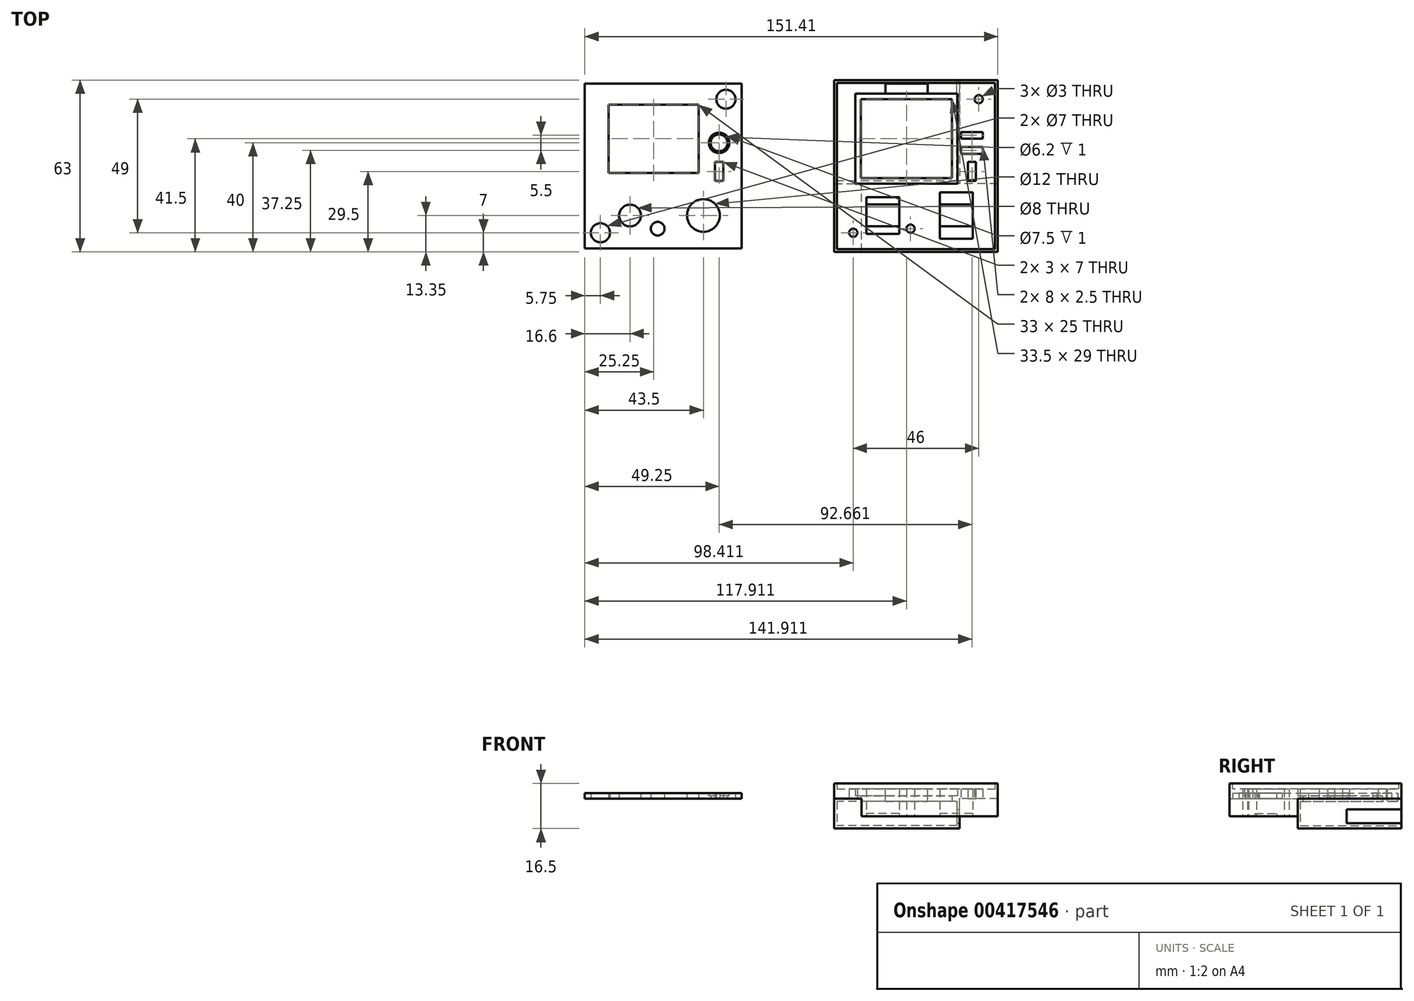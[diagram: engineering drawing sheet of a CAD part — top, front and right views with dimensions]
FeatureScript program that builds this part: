
annotation { "Feature Type Name" : "Feature", "Feature Type Description" : "" }
export const myFeature = defineFeature(function(context is Context, id is Id, definition is map)
    precondition{}
    {
        {
            var Q0;
            Q0=qCreatedBy(makeId("Top.planeOp"),FACE);
            var sketch = newSketch(context, id + "F0", { "sketchPlane" : qUnion([Q0])});
            skPoint(sketch, "E0.middle", {"position": v(0, 0) * mm});
            skLineSegment(sketch, "E1.bottom", {"start": v(13, -2.5) * mm, "end": v(-20, -2.5) * mm});
            skLineSegment(sketch, "E1.top", {"start": v(13, 22.5) * mm, "end": v(-20, 22.5) * mm});
            skLineSegment(sketch, "E1.left", {"start": v(13, -2.5) * mm, "end": v(13, 22.5) * mm});
            skLineSegment(sketch, "E1.right", {"start": v(-20, -2.5) * mm, "end": v(-20, 22.5) * mm});
            skCircle(sketch, "E2", {"center": v(14.75, -18.15) * mm, "radius": 6 * mm});
            skCircle(sketch, "E3", {"center": v(-12.15, -18.15) * mm, "radius": 4 * mm});
            skCircle(sketch, "E4", {"center": v(-2, -23) * mm, "radius": 2.5 * mm});
            skPoint(sketch, "E5", {"position": v(-3.5, 10) * mm});
            skPoint(sketch, "E5.positionSnap0", {"position": v(-3.5, 22.5) * mm});
            skPoint(sketch, "E5.positionSnap1", {"position": v(-20, 10) * mm});
            skCircle(sketch, "E6", {"center": v(-23, -24.5) * mm, "radius": 3.5 * mm});
            skCircle(sketch, "E7", {"center": v(23, 24.5) * mm, "radius": 3.5 * mm});
            skLineSegment(sketch, "E8.bottom", {"start": v(28.75, -30.25) * mm, "end": v(-28.75, -30.25) * mm});
            skLineSegment(sketch, "E8.top", {"start": v(28.75, 30.25) * mm, "end": v(-28.75, 30.25) * mm});
            skLineSegment(sketch, "E8.left", {"start": v(28.75, -30.25) * mm, "end": v(28.75, 30.25) * mm});
            skLineSegment(sketch, "E8.right", {"start": v(-28.75, -30.25) * mm, "end": v(-28.75, 30.25) * mm});
            skCircle(sketch, "E9", {"center": v(20.5, 8.5) * mm, "radius": 3.75 * mm, "construction": true});
            skCircle(sketch, "E10", {"center": v(20.5, 8.5) * mm, "radius": 3.1 * mm});
            skLineSegment(sketch, "E11.bottom", {"start": v(22, -5.5) * mm, "end": v(19, -5.5) * mm});
            skLineSegment(sketch, "E11.top", {"start": v(22, 1.5) * mm, "end": v(19, 1.5) * mm});
            skLineSegment(sketch, "E11.left", {"start": v(22, -5.5) * mm, "end": v(22, 1.5) * mm});
            skLineSegment(sketch, "E11.right", {"start": v(19, -5.5) * mm, "end": v(19, 1.5) * mm});
            skPoint(sketch, "E11.middle", {"position": v(20.5, -2) * mm});
            skSolve(sketch);
        }
        {
            var Q0;
            Q0=qCreatedBy(makeId("Top.planeOp"),FACE);
            var sketch = newSketch(context, id + "F1", { "sketchPlane" : qUnion([Q0])});
            skLineSegment(sketch, "E12.bottom", {"start": v(122.66, -31.5) * mm, "end": v(62.66, -31.5) * mm});
            skLineSegment(sketch, "E12.top", {"start": v(122.66, 31.5) * mm, "end": v(62.66, 31.5) * mm});
            skLineSegment(sketch, "E12.left", {"start": v(122.66, -31.5) * mm, "end": v(122.66, 31.5) * mm});
            skLineSegment(sketch, "E12.right", {"start": v(62.66, -31.5) * mm, "end": v(62.66, 31.5) * mm});
            skPoint(sketch, "E12.middle", {"position": v(92.66, 0) * mm});
            skLineSegment(sketch, "E13.bottom", {"start": v(107.91, -6.5) * mm, "end": v(70.41, -6.5) * mm});
            skLineSegment(sketch, "E13.top", {"start": v(107.91, 26.5) * mm, "end": v(70.41, 26.5) * mm});
            skLineSegment(sketch, "E13.left", {"start": v(107.91, -6.5) * mm, "end": v(107.91, 26.5) * mm});
            skLineSegment(sketch, "E13.right", {"start": v(70.41, -6.5) * mm, "end": v(70.41, 26.5) * mm});
            skCircle(sketch, "E14", {"center": v(69.66, -24.5) * mm, "radius": 1.5 * mm});
            skCircle(sketch, "E15", {"center": v(115.66, 24.5) * mm, "radius": 1.5 * mm});
            skCircle(sketch, "E16", {"center": v(107.41, -18.15) * mm, "radius": 6.1 * mm, "construction": true});
            skLineSegment(sketch, "E17.bottom", {"start": v(111.66, 1.5) * mm, "end": v(114.66, 1.5) * mm});
            skLineSegment(sketch, "E17.top", {"start": v(111.66, -5.5) * mm, "end": v(114.66, -5.5) * mm});
            skLineSegment(sketch, "E17.left", {"start": v(111.66, 1.5) * mm, "end": v(111.66, -5.5) * mm});
            skLineSegment(sketch, "E17.right", {"start": v(114.66, 1.5) * mm, "end": v(114.66, -5.5) * mm});
            skPoint(sketch, "E18.centerSnap0", {"position": v(113.16, 1.5) * mm});
            skCircle(sketch, "E19", {"center": v(80.51, -18.15) * mm, "radius": 2.5 * mm, "construction": true});
            skCircle(sketch, "E20", {"center": v(90.66, -23) * mm, "radius": 1.5 * mm});
            skLineSegment(sketch, "E21.bottom", {"start": v(113.41, -26.65) * mm, "end": v(101.41, -26.65) * mm});
            skLineSegment(sketch, "E21.top", {"start": v(113.41, -9.65) * mm, "end": v(101.41, -9.65) * mm});
            skLineSegment(sketch, "E21.left", {"start": v(113.41, -26.65) * mm, "end": v(113.41, -9.65) * mm});
            skLineSegment(sketch, "E21.right", {"start": v(101.41, -26.65) * mm, "end": v(101.41, -9.65) * mm});
            skLineSegment(sketch, "E22.bottom", {"start": v(115.66, 6) * mm, "end": v(110.66, 6) * mm, "construction": true});
            skLineSegment(sketch, "E22.top", {"start": v(115.66, 11) * mm, "end": v(110.66, 11) * mm, "construction": true});
            skLineSegment(sketch, "E22.left", {"start": v(115.66, 6) * mm, "end": v(115.66, 11) * mm, "construction": true});
            skLineSegment(sketch, "E22.right", {"start": v(110.66, 6) * mm, "end": v(110.66, 11) * mm, "construction": true});
            skPoint(sketch, "E22.middle", {"position": v(113.16, 8.5) * mm});
            skPoint(sketch, "E23", {"position": v(89.16, 10) * mm});
            skPoint(sketch, "E23.positionSnap0", {"position": v(89.16, 26.5) * mm});
            skPoint(sketch, "E23.positionSnap1", {"position": v(70.41, 10) * mm});
            skLineSegment(sketch, "E24.bottom", {"start": v(117.16, 4.5) * mm, "end": v(109.16, 4.5) * mm});
            skLineSegment(sketch, "E24.top", {"start": v(117.16, 12.5) * mm, "end": v(109.16, 12.5) * mm});
            skLineSegment(sketch, "E24.left", {"start": v(117.16, 4.5) * mm, "end": v(117.16, 12.5) * mm});
            skLineSegment(sketch, "E24.right", {"start": v(109.16, 4.5) * mm, "end": v(109.16, 12.5) * mm});
            skCircle(sketch, "E25", {"center": v(69.66, -24.5) * mm, "radius": 3.5 * mm, "construction": true});
            skCircle(sketch, "E26", {"center": v(115.66, 24.5) * mm, "radius": 3.5 * mm, "construction": true});
            skLineSegment(sketch, "E27.bottom", {"start": v(121.41, -30.25) * mm, "end": v(63.91, -30.25) * mm, "construction": true});
            skLineSegment(sketch, "E27.top", {"start": v(121.41, 30.25) * mm, "end": v(63.91, 30.25) * mm, "construction": true});
            skLineSegment(sketch, "E27.left", {"start": v(121.41, -30.25) * mm, "end": v(121.41, 30.25) * mm, "construction": true});
            skLineSegment(sketch, "E27.right", {"start": v(63.91, -30.25) * mm, "end": v(63.91, 30.25) * mm, "construction": true});
            skLineSegment(sketch, "E28.bottom", {"start": v(86.51, -24.9) * mm, "end": v(74.51, -24.9) * mm});
            skLineSegment(sketch, "E28.top", {"start": v(86.51, -11.4) * mm, "end": v(74.51, -11.4) * mm});
            skLineSegment(sketch, "E28.left", {"start": v(86.51, -24.9) * mm, "end": v(86.51, -11.4) * mm});
            skLineSegment(sketch, "E28.right", {"start": v(74.51, -24.9) * mm, "end": v(74.51, -11.4) * mm});
            skLineSegment(sketch, "E29.bottom", {"start": v(86.51, -22.15) * mm, "end": v(74.51, -22.15) * mm});
            skLineSegment(sketch, "E29.top", {"start": v(86.51, -14.15) * mm, "end": v(74.51, -14.15) * mm});
            skLineSegment(sketch, "E29.left", {"start": v(86.51, -22.15) * mm, "end": v(86.51, -14.15) * mm});
            skLineSegment(sketch, "E29.right", {"start": v(74.51, -22.15) * mm, "end": v(74.51, -14.15) * mm});
            skLineSegment(sketch, "E30.bottom", {"start": v(113.41, -22.15) * mm, "end": v(101.41, -22.15) * mm});
            skLineSegment(sketch, "E30.top", {"start": v(113.41, -14.15) * mm, "end": v(101.41, -14.15) * mm});
            skLineSegment(sketch, "E30.left", {"start": v(113.41, -22.15) * mm, "end": v(113.41, -14.15) * mm});
            skLineSegment(sketch, "E30.right", {"start": v(101.41, -22.15) * mm, "end": v(101.41, -14.15) * mm});
            skLineSegment(sketch, "E31.bottom", {"start": v(117.16, 7) * mm, "end": v(109.16, 7) * mm});
            skLineSegment(sketch, "E31.top", {"start": v(117.16, 10) * mm, "end": v(109.16, 10) * mm});
            skLineSegment(sketch, "E31.left", {"start": v(117.16, 7) * mm, "end": v(117.16, 10) * mm});
            skLineSegment(sketch, "E31.right", {"start": v(109.16, 7) * mm, "end": v(109.16, 10) * mm});
            skSolve(sketch);
        }
        {
            var Q0;
            Q0=makeQuery(id+"F1.imprint","IMPRINT",FACE,{"disambiguationData":[TD([[makeQuery(id+"F1.imprint","IMPRINT",EDGE,{"derivedFrom":sQuery(id+"F1.wireOp",EDGE,"E12.bottom")}),-1.0]])]});
            var Q1;
            Q1=makeQuery(id+"F1.imprint","IMPRINT",FACE,{"disambiguationData":[TD([[makeQuery(id+"F1.imprint","IMPRINT",EDGE,{"derivedFrom":sQuery(id+"F1.wireOp",EDGE,"E29.bottom")}),-1.0]])]});
            var Q2;
            Q2=makeQuery(id+"F1.imprint","IMPRINT",FACE,{"disambiguationData":[TD([[makeQuery(id+"F1.imprint","IMPRINT",EDGE,{"derivedFrom":sQuery(id+"F1.wireOp",EDGE,"E30.bottom")}),-1.0]])]});
            var Q3;
            Q3=makeQuery(id+"F1.imprint","IMPRINT",FACE,{"disambiguationData":[TD([[makeQuery(id+"F1.imprint","IMPRINT",EDGE,{"derivedFrom":sQuery(id+"F1.wireOp",EDGE,"E31.bottom")}),-1.0]])]});
            extrude(context, id + "F2", {"entities" : qUnion([Q0, Q1, Q2, Q3]), "depth" : 3.5 * mm});
        }
        {
            var Q0;
            Q0=makeQuery(id+"F2.opExtrude","CAP_FACE",FACE,{"disambiguationData":[OSD([sQuery(id+"F1.wireOp",EDGE,"E12.bottom"),sQuery(id+"F1.wireOp",EDGE,"E12.top"),sQuery(id+"F1.wireOp",EDGE,"E12.left"),sQuery(id+"F1.wireOp",EDGE,"E12.right"),sQuery(id+"F1.wireOp",EDGE,"E13.bottom"),sQuery(id+"F1.wireOp",EDGE,"E13.top"),sQuery(id+"F1.wireOp",EDGE,"E13.left"),sQuery(id+"F1.wireOp",EDGE,"E13.right"),sQuery(id+"F1.wireOp",EDGE,"E14"),sQuery(id+"F1.wireOp",EDGE,"E15"),sQuery(id+"F1.wireOp",EDGE,"E16"),sQuery(id+"F1.wireOp",EDGE,"E17.bottom"),sQuery(id+"F1.wireOp",EDGE,"E17.top"),sQuery(id+"F1.wireOp",EDGE,"E17.left"),sQuery(id+"F1.wireOp",EDGE,"E17.right"),sQuery(id+"F1.wireOp",EDGE,"E18"),sQuery(id+"F1.wireOp",EDGE,"E19"),sQuery(id+"F1.wireOp",EDGE,"E20")])],"isStart":false});
            var sketch = newSketch(context, id + "F3", { "sketchPlane" : qUnion([Q0])});
            skLineSegment(sketch, "E32.bottom", {"start": v(96.91, 26.5) * mm, "end": v(81.41, 26.5) * mm});
            skLineSegment(sketch, "E32.top", {"start": v(96.91, 30.25) * mm, "end": v(81.41, 30.25) * mm});
            skLineSegment(sketch, "E32.left", {"start": v(96.91, 26.5) * mm, "end": v(96.91, 30.25) * mm});
            skLineSegment(sketch, "E32.right", {"start": v(81.41, 26.5) * mm, "end": v(81.41, 30.25) * mm});
            skPoint(sketch, "E32.middle", {"position": v(89.16, 28.38) * mm});
            skPoint(sketch, "E32.middle.positionSnap0", {"position": v(89.16, 26.5) * mm});
            skPoint(sketch, "E32.centerSnap0", {"position": v(89.16, 26.5) * mm});
            skSolve(sketch);
        }
        {
            var Q0;
            Q0=makeQuery(id+"F2.opExtrude","CAP_FACE",FACE,{"disambiguationData":[OSD([sQuery(id+"F1.wireOp",EDGE,"E12.bottom"),sQuery(id+"F1.wireOp",EDGE,"E12.top"),sQuery(id+"F1.wireOp",EDGE,"E12.left"),sQuery(id+"F1.wireOp",EDGE,"E12.right"),sQuery(id+"F1.wireOp",EDGE,"E13.bottom"),sQuery(id+"F1.wireOp",EDGE,"E13.top"),sQuery(id+"F1.wireOp",EDGE,"E13.left"),sQuery(id+"F1.wireOp",EDGE,"E13.right"),sQuery(id+"F1.wireOp",EDGE,"E14"),sQuery(id+"F1.wireOp",EDGE,"E15"),sQuery(id+"F1.wireOp",EDGE,"E16"),sQuery(id+"F1.wireOp",EDGE,"E17.bottom"),sQuery(id+"F1.wireOp",EDGE,"E17.top"),sQuery(id+"F1.wireOp",EDGE,"E17.left"),sQuery(id+"F1.wireOp",EDGE,"E17.right"),sQuery(id+"F1.wireOp",EDGE,"E18"),sQuery(id+"F1.wireOp",EDGE,"E19"),sQuery(id+"F1.wireOp",EDGE,"E20")])],"isStart":true});
            var sketch = newSketch(context, id + "F4", { "sketchPlane" : qUnion([Q0])});
            skLineSegment(sketch, "E33.bottom", {"start": v(70.41, -26.5) * mm, "end": v(107.91, -26.5) * mm});
            skLineSegment(sketch, "E33.top", {"start": v(70.41, 6.5) * mm, "end": v(107.91, 6.5) * mm});
            skLineSegment(sketch, "E33.left", {"start": v(70.41, -26.5) * mm, "end": v(70.41, 6.5) * mm});
            skLineSegment(sketch, "E33.right", {"start": v(107.91, -26.5) * mm, "end": v(107.91, 6.5) * mm});
            skLineSegment(sketch, "E34.0", {"start": v(105.91, -24.5) * mm, "end": v(105.91, 4.5) * mm});
            skLineSegment(sketch, "E34.1", {"start": v(72.41, -24.5) * mm, "end": v(105.91, -24.5) * mm});
            skLineSegment(sketch, "E34.2", {"start": v(72.41, -24.5) * mm, "end": v(72.41, 4.5) * mm});
            skLineSegment(sketch, "E34.3", {"start": v(72.41, 4.5) * mm, "end": v(105.91, 4.5) * mm});
            skSolve(sketch);
        }
        {
            var Q0;
            Q0=makeQuery(id+"F4.imprint","IMPRINT",FACE,{"disambiguationData":[TD([[makeQuery(id+"F4.imprint","IMPRINT",EDGE,{"derivedFrom":sQuery(id+"F4.wireOp",EDGE,"E33.bottom")}),-1.0]])]});
            extrude(context, id + "F5", {"entities" : qUnion([Q0]), "operationType" : NewBodyOperationType.ADD, "oppositeDirection" : true, "depth" : 1 * mm});
        }
        {
            var Q0;
            Q0=makeQuery(id+"F3.imprint","IMPRINT",FACE,{"disambiguationData":[TD([[makeQuery(id+"F3.imprint","IMPRINT",EDGE,{"derivedFrom":sQuery(id+"F3.wireOp",EDGE,"E32.bottom")}),-1.0]])]});
            extrude(context, id + "F6", {"entities" : qUnion([Q0]), "operationType" : NewBodyOperationType.REMOVE, "oppositeDirection" : true, "depth" : 2.5 * mm});
        }
        {
            var Q0;
            Q0=makeQuery(id+"F5.boolean.opBoolean","MERGE",FACE,{"derivedFrom":[makeQuery(id+"F2.opExtrude","CAP_FACE",FACE,{"disambiguationData":[OSD([sQuery(id+"F1.wireOp",EDGE,"E12.bottom"),sQuery(id+"F1.wireOp",EDGE,"E12.top"),sQuery(id+"F1.wireOp",EDGE,"E12.left"),sQuery(id+"F1.wireOp",EDGE,"E12.right"),sQuery(id+"F1.wireOp",EDGE,"E13.bottom"),sQuery(id+"F1.wireOp",EDGE,"E13.top"),sQuery(id+"F1.wireOp",EDGE,"E13.left"),sQuery(id+"F1.wireOp",EDGE,"E13.right"),sQuery(id+"F1.wireOp",EDGE,"E14"),sQuery(id+"F1.wireOp",EDGE,"E15"),sQuery(id+"F1.wireOp",EDGE,"E16"),sQuery(id+"F1.wireOp",EDGE,"E17.bottom"),sQuery(id+"F1.wireOp",EDGE,"E17.top"),sQuery(id+"F1.wireOp",EDGE,"E17.left"),sQuery(id+"F1.wireOp",EDGE,"E17.right"),sQuery(id+"F1.wireOp",EDGE,"E18"),sQuery(id+"F1.wireOp",EDGE,"E19"),sQuery(id+"F1.wireOp",EDGE,"E20")])],"isStart":true}),makeQuery(id+"F5.opExtrude","CAP_FACE",FACE,{"disambiguationData":[OSD([sQuery(id+"F4.wireOp",EDGE,"E33.bottom"),sQuery(id+"F4.wireOp",EDGE,"E33.top"),sQuery(id+"F4.wireOp",EDGE,"E33.left"),sQuery(id+"F4.wireOp",EDGE,"E33.right"),sQuery(id+"F4.wireOp",EDGE,"E34.0"),sQuery(id+"F4.wireOp",EDGE,"E34.1"),sQuery(id+"F4.wireOp",EDGE,"E34.2"),sQuery(id+"F4.wireOp",EDGE,"E34.3")])],"isStart":true})]});
            var sketch = newSketch(context, id + "F7", { "sketchPlane" : qUnion([Q0])});
            skLineSegment(sketch, "E35.bottom", {"start": v(114.91, -31.5) * mm, "end": v(67.91, -31.5) * mm, "construction": true});
            skLineSegment(sketch, "E35.top", {"start": v(114.91, 0.5) * mm, "end": v(67.91, 0.5) * mm, "construction": true});
            skLineSegment(sketch, "E35.left", {"start": v(114.91, -31.5) * mm, "end": v(114.91, 0.5) * mm, "construction": true});
            skLineSegment(sketch, "E35.right", {"start": v(67.91, -31.5) * mm, "end": v(67.91, 0.5) * mm, "construction": true});
            skSolve(sketch);
        }
        {
            var Q0;
            Q0=makeQuery(id+"F0.imprint","IMPRINT",FACE,{"disambiguationData":[TD([[makeQuery(id+"F0.imprint","IMPRINT",EDGE,{"derivedFrom":sQuery(id+"F0.wireOp",EDGE,"E1.bottom")}),1.0]])]});
            var Q1;
            {var subQ3=sQuery(id+"F0.wireOp",EDGE,"XrDQp62H-MWh6-TRDE-LRBF-NnkS5WIpAHLl.bottom");Q1=makeQuery(id+"F0.imprint","IMPRINT",FACE,{"disambiguationData":[TD([[makeQuery(id+"F0.imprint","IMPRINT",EDGE,{"derivedFrom":subQ3}),-1.0]])]});}
            var Q2;
            {var subQ0=sQuery(id+"F0.wireOp",EDGE,"2c6vpU0J-e8TA-CdwJ-wqkp-RvG89t70vTgT.bottom");Q2=makeQuery(id+"F0.imprint","IMPRINT",FACE,{"disambiguationData":[TD([[makeQuery(id+"F0.imprint","IMPRINT",EDGE,{"derivedFrom":subQ0}),1.0]])]});}
            var Q3;
            {var subQ3=sQuery(id+"F0.wireOp",EDGE,"BUTc56Jz-DEV2-YpXM-oIQJ-WA8c8EbTXwWs.bottom");Q3=makeQuery(id+"F0.imprint","IMPRINT",FACE,{"disambiguationData":[TD([[makeQuery(id+"F0.imprint","IMPRINT",EDGE,{"derivedFrom":subQ3}),1.0]])]});}
            var Q4;
            {var subQ0=sQuery(id+"F0.wireOp",EDGE,"JL6GV5r3-Ixaj-ni79-uZlj-3xSKczFOYfCu.bottom");Q4=makeQuery(id+"F0.imprint","IMPRINT",FACE,{"disambiguationData":[TD([[makeQuery(id+"F0.imprint","IMPRINT",EDGE,{"derivedFrom":subQ0}),-1.0]])]});}
            extrude(context, id + "F8", {"entities" : qUnion([Q0, Q1, Q2, Q3, Q4]), "depth" : 2 * mm});
        }
        {
            var Q0;
            Q0=makeQuery(id+"F8.opExtrude","CAP_FACE",FACE,{"disambiguationData":[OSD([sQuery(id+"F0.wireOp",EDGE,"E1.bottom"),sQuery(id+"F0.wireOp",EDGE,"E1.top"),sQuery(id+"F0.wireOp",EDGE,"E1.left"),sQuery(id+"F0.wireOp",EDGE,"E1.right"),sQuery(id+"F0.wireOp",EDGE,"2c6vpU0J-e8TA-CdwJ-wqkp-RvG89t70vTgT.top"),sQuery(id+"F0.wireOp",EDGE,"JL6GV5r3-Ixaj-ni79-uZlj-3xSKczFOYfCu.top"),sQuery(id+"F0.wireOp",EDGE,"XrDQp62H-MWh6-TRDE-LRBF-NnkS5WIpAHLl.bottom"),sQuery(id+"F0.wireOp",EDGE,"XrDQp62H-MWh6-TRDE-LRBF-NnkS5WIpAHLl.top"),sQuery(id+"F0.wireOp",EDGE,"XrDQp62H-MWh6-TRDE-LRBF-NnkS5WIpAHLl.right"),sQuery(id+"F0.wireOp",EDGE,"BUTc56Jz-DEV2-YpXM-oIQJ-WA8c8EbTXwWs.bottom"),sQuery(id+"F0.wireOp",EDGE,"BUTc56Jz-DEV2-YpXM-oIQJ-WA8c8EbTXwWs.top"),sQuery(id+"F0.wireOp",EDGE,"BUTc56Jz-DEV2-YpXM-oIQJ-WA8c8EbTXwWs.right"),sQuery(id+"F0.wireOp",EDGE,"E2"),sQuery(id+"F0.wireOp",EDGE,"E3"),sQuery(id+"F0.wireOp",EDGE,"E4")])],"isStart":false});
            var sketch = newSketch(context, id + "F9", { "sketchPlane" : qUnion([Q0])});
            skLineSegment(sketch, "E36.bottom", {"start": v(-20, 22.5) * mm, "end": v(13, 22.5) * mm});
            skLineSegment(sketch, "E36.top", {"start": v(-20, 23.5) * mm, "end": v(13, 23.5) * mm});
            skLineSegment(sketch, "E36.left", {"start": v(-20, 22.5) * mm, "end": v(-20, 23.5) * mm});
            skLineSegment(sketch, "E36.right", {"start": v(13, 22.5) * mm, "end": v(13, 23.5) * mm});
            skLineSegment(sketch, "E37.bottom", {"start": v(-20, 23.5) * mm, "end": v(-21, 23.5) * mm});
            skLineSegment(sketch, "E37.top", {"start": v(-20, -2.5) * mm, "end": v(-21, -2.5) * mm});
            skLineSegment(sketch, "E37.left", {"start": v(-20, 23.5) * mm, "end": v(-20, -2.5) * mm});
            skLineSegment(sketch, "E37.right", {"start": v(-21, 23.5) * mm, "end": v(-21, -2.5) * mm});
            skLineSegment(sketch, "E38.bottom", {"start": v(13, 23.5) * mm, "end": v(14, 23.5) * mm});
            skLineSegment(sketch, "E38.top", {"start": v(13, -2.5) * mm, "end": v(14, -2.5) * mm});
            skLineSegment(sketch, "E38.left", {"start": v(13, 23.5) * mm, "end": v(13, -2.5) * mm});
            skLineSegment(sketch, "E38.right", {"start": v(14, 23.5) * mm, "end": v(14, -2.5) * mm});
            skLineSegment(sketch, "E39.bottom", {"start": v(-21, -2.5) * mm, "end": v(14, -2.5) * mm});
            skLineSegment(sketch, "E39.top", {"start": v(-21, -3.5) * mm, "end": v(14, -3.5) * mm});
            skLineSegment(sketch, "E39.left", {"start": v(-21, -2.5) * mm, "end": v(-21, -3.5) * mm});
            skLineSegment(sketch, "E39.right", {"start": v(14, -2.5) * mm, "end": v(14, -3.5) * mm});
            skSolve(sketch);
        }
        {
            var Q0;
            Q0=makeQuery(id+"F7.imprint","IMPRINT",FACE,{"disambiguationData":[TD([[makeQuery(id+"F7.imprint","IMPRINT",EDGE,{"derivedFrom":makeQuery(id+"F2.opExtrude","CAP_EDGE",EDGE,{"disambiguationData":[OSD([sQuery(id+"F1.wireOp",EDGE,"E12.bottom")])],"isStart":true})}),1.0]])]});
            var sketch = newSketch(context, id + "F10", { "sketchPlane" : qUnion([Q0])});
            skPoint(sketch, "E40.0", {"position": v(62.66, -31.5) * mm});
            skPoint(sketch, "E41.0", {"position": v(122.66, -31.5) * mm});
            skLineSegment(sketch, "E42.bottom", {"start": v(62.66, -31.5) * mm, "end": v(108.66, -31.5) * mm});
            skLineSegment(sketch, "E42.top", {"start": v(62.66, 6.5) * mm, "end": v(108.66, 6.5) * mm});
            skLineSegment(sketch, "E42.left", {"start": v(62.66, -31.5) * mm, "end": v(62.66, 6.5) * mm});
            skLineSegment(sketch, "E42.right", {"start": v(108.66, -31.5) * mm, "end": v(108.66, 6.5) * mm});
            skSolve(sketch);
        }
        {
            var Q0;
            Q0 = qSketchRegion(id + "F10", true);
            extrude(context, id + "F11", {"entities" : qUnion([Q0]), "operationType" : NewBodyOperationType.ADD, "depth" : 11 * mm});
        }
        {
            var Q0;
            Q0=makeQuery(id+"F11.boolean.opBoolean","MERGE",FACE,{"derivedFrom":[makeQuery(id+"F2.opExtrude","SWEPT_FACE",FACE,{"disambiguationData":[OSD([sQuery(id+"F1.wireOp",EDGE,"E12.top")])]}),makeQuery(id+"F11.opExtrude","SWEPT_FACE",FACE,{"disambiguationData":[OSD([sQuery(id+"F10.wireOp",EDGE,"E42.bottom")])]})]});
            var sketch = newSketch(context, id + "F12", { "sketchPlane" : qUnion([Q0])});
            skLineSegment(sketch, "E43.bottom", {"start": v(-107.66, -1) * mm, "end": v(-63.66, -1) * mm});
            skLineSegment(sketch, "E43.top", {"start": v(-107.66, -10) * mm, "end": v(-63.66, -10) * mm});
            skLineSegment(sketch, "E43.left", {"start": v(-107.66, -1) * mm, "end": v(-107.66, -10) * mm});
            skLineSegment(sketch, "E43.right", {"start": v(-63.66, -1) * mm, "end": v(-63.66, -10) * mm});
            skSolve(sketch);
        }
        {
            var Q0;
            Q0 = qSketchRegion(id + "F12", true);
            extrude(context, id + "F13", {"entities" : qUnion([Q0]), "operationType" : NewBodyOperationType.REMOVE, "oppositeDirection" : true, "depth" : 37 * mm});
        }
        {
            var Q0;
            Q0=makeQuery(id+"F11.boolean.opBoolean","MERGE",FACE,{"derivedFrom":[makeQuery(id+"F2.opExtrude","SWEPT_FACE",FACE,{"disambiguationData":[OSD([sQuery(id+"F1.wireOp",EDGE,"E12.top")])]}),makeQuery(id+"F11.opExtrude","SWEPT_FACE",FACE,{"disambiguationData":[OSD([sQuery(id+"F10.wireOp",EDGE,"E42.bottom")])]})]});
            var sketch = newSketch(context, id + "F14", { "sketchPlane" : qUnion([Q0])});
            skLineSegment(sketch, "E44.bottom", {"start": v(-107.66, -9) * mm, "end": v(-108.66, -9) * mm});
            skLineSegment(sketch, "E44.top", {"start": v(-107.66, -4) * mm, "end": v(-108.66, -4) * mm});
            skLineSegment(sketch, "E44.left", {"start": v(-107.66, -9) * mm, "end": v(-107.66, -4) * mm});
            skLineSegment(sketch, "E44.right", {"start": v(-108.66, -9) * mm, "end": v(-108.66, -4) * mm});
            skSolve(sketch);
        }
        {
            var Q0;
            Q0 = qSketchRegion(id + "F14", true);
            extrude(context, id + "F15", {"entities" : qUnion([Q0]), "operationType" : NewBodyOperationType.REMOVE, "oppositeDirection" : true, "depth" : 20 * mm});
        }
        {
            var Q0;
            Q0=makeQuery(id+"F6.boolean.opBoolean","MERGE",FACE,{"derivedFrom":[makeQuery(id+"F5.opExtrude","CAP_FACE",FACE,{"disambiguationData":[OSD([sQuery(id+"F4.wireOp",EDGE,"E33.bottom"),sQuery(id+"F4.wireOp",EDGE,"E33.top"),sQuery(id+"F4.wireOp",EDGE,"E33.left"),sQuery(id+"F4.wireOp",EDGE,"E33.right"),sQuery(id+"F4.wireOp",EDGE,"E34.0"),sQuery(id+"F4.wireOp",EDGE,"E34.1"),sQuery(id+"F4.wireOp",EDGE,"E34.2"),sQuery(id+"F4.wireOp",EDGE,"E34.3")])],"isStart":false}),makeQuery(id+"F6.opExtrude","CAP_FACE",FACE,{"disambiguationData":[OSD([sQuery(id+"F3.wireOp",EDGE,"E32.bottom"),sQuery(id+"F3.wireOp",EDGE,"E32.top"),sQuery(id+"F3.wireOp",EDGE,"E32.left"),sQuery(id+"F3.wireOp",EDGE,"E32.right")])],"isStart":false})]});
            var sketch = newSketch(context, id + "F16", { "sketchPlane" : qUnion([Q0])});
            skPoint(sketch, "E45.0", {"position": v(72.41, 24.5) * mm});
            skPoint(sketch, "E45.1", {"position": v(105.91, -4.5) * mm});
            skLineSegment(sketch, "E46.bottom", {"start": v(72.41, 24.5) * mm, "end": v(105.91, 24.5) * mm});
            skLineSegment(sketch, "E46.top", {"start": v(72.41, -4.5) * mm, "end": v(105.91, -4.5) * mm});
            skLineSegment(sketch, "E46.left", {"start": v(72.41, -4.5) * mm, "end": v(72.41, 24.5) * mm});
            skLineSegment(sketch, "E46.right", {"start": v(105.91, -4.5) * mm, "end": v(105.91, 24.5) * mm});
            skLineSegment(sketch, "E47.bottom", {"start": v(81.41, 30.25) * mm, "end": v(96.91, 30.25) * mm});
            skLineSegment(sketch, "E47.top", {"start": v(81.41, 26.5) * mm, "end": v(96.91, 26.5) * mm});
            skLineSegment(sketch, "E47.left", {"start": v(81.41, 30.25) * mm, "end": v(81.41, 26.5) * mm});
            skLineSegment(sketch, "E47.right", {"start": v(96.91, 30.25) * mm, "end": v(96.91, 26.5) * mm});
            skSolve(sketch);
        }
        {
            var Q0;
            Q0 = qSketchRegion(id + "F16", true);
            extrude(context, id + "F17", {"entities" : qUnion([Q0]), "operationType" : NewBodyOperationType.REMOVE, "oppositeDirection" : true, "depth" : 4 * mm});
        }
        {
            var Q0;
            Q0=makeQuery(id+"F2.opExtrude","CAP_FACE",FACE,{"disambiguationData":[OSD([sQuery(id+"F1.wireOp",EDGE,"E12.bottom"),sQuery(id+"F1.wireOp",EDGE,"E12.top"),sQuery(id+"F1.wireOp",EDGE,"E12.left"),sQuery(id+"F1.wireOp",EDGE,"E12.right"),sQuery(id+"F1.wireOp",EDGE,"E13.bottom"),sQuery(id+"F1.wireOp",EDGE,"E13.top"),sQuery(id+"F1.wireOp",EDGE,"E13.left"),sQuery(id+"F1.wireOp",EDGE,"E13.right"),sQuery(id+"F1.wireOp",EDGE,"E14"),sQuery(id+"F1.wireOp",EDGE,"E15"),sQuery(id+"F1.wireOp",EDGE,"E17.bottom"),sQuery(id+"F1.wireOp",EDGE,"E17.top"),sQuery(id+"F1.wireOp",EDGE,"E17.left"),sQuery(id+"F1.wireOp",EDGE,"E17.right"),sQuery(id+"F1.wireOp",EDGE,"E19"),sQuery(id+"F1.wireOp",EDGE,"E20"),sQuery(id+"F1.wireOp",EDGE,"E21.bottom"),sQuery(id+"F1.wireOp",EDGE,"E21.top"),sQuery(id+"F1.wireOp",EDGE,"E21.left"),sQuery(id+"F1.wireOp",EDGE,"E21.right"),sQuery(id+"F1.wireOp",EDGE,"E24.bottom"),sQuery(id+"F1.wireOp",EDGE,"E24.top"),sQuery(id+"F1.wireOp",EDGE,"E24.left"),sQuery(id+"F1.wireOp",EDGE,"E24.right")])],"isStart":false});
            var sketch = newSketch(context, id + "F18", { "sketchPlane" : qUnion([Q0])});
            skLineSegment(sketch, "E48.bottom", {"start": v(62.66, 31.5) * mm, "end": v(122.66, 31.5) * mm});
            skLineSegment(sketch, "E48.top", {"start": v(62.66, -31.5) * mm, "end": v(122.66, -31.5) * mm});
            skLineSegment(sketch, "E48.left", {"start": v(62.66, 31.5) * mm, "end": v(62.66, -31.5) * mm});
            skLineSegment(sketch, "E48.right", {"start": v(122.66, 31.5) * mm, "end": v(122.66, -31.5) * mm});
            skLineSegment(sketch, "E49.0", {"start": v(63.66, -30.5) * mm, "end": v(121.66, -30.5) * mm});
            skLineSegment(sketch, "E49.1", {"start": v(63.66, 30.5) * mm, "end": v(63.66, -30.5) * mm});
            skLineSegment(sketch, "E49.2", {"start": v(63.66, 30.5) * mm, "end": v(121.66, 30.5) * mm});
            skLineSegment(sketch, "E49.3", {"start": v(121.66, 30.5) * mm, "end": v(121.66, -30.5) * mm});
            skSolve(sketch);
        }
        {
            var Q0;
            Q0 = qSketchRegion(id + "F18", true);
            extrude(context, id + "F19", {"entities" : qUnion([Q0]), "operationType" : NewBodyOperationType.ADD, "depth" : 2 * mm});
        }
        {
            var Q0;
            Q0=makeQuery(id+"F7.imprint","IMPRINT",FACE,{"disambiguationData":[TD([[makeQuery(id+"F7.imprint","IMPRINT",EDGE,{"derivedFrom":makeQuery(id+"F2.opExtrude","CAP_EDGE",EDGE,{"disambiguationData":[OSD([sQuery(id+"F1.wireOp",EDGE,"E12.bottom")])],"isStart":true})}),1.0]])]});
            var sketch = newSketch(context, id + "F20", { "sketchPlane" : qUnion([Q0])});
            skPoint(sketch, "E50.0", {"position": v(122.66, 31.5) * mm});
            skLineSegment(sketch, "E51.bottom", {"start": v(122.66, 31.5) * mm, "end": v(72.66, 31.5) * mm});
            skLineSegment(sketch, "E51.top", {"start": v(122.66, 6.5) * mm, "end": v(72.66, 6.5) * mm});
            skLineSegment(sketch, "E51.left", {"start": v(122.66, 31.5) * mm, "end": v(122.66, 6.5) * mm});
            skLineSegment(sketch, "E51.right", {"start": v(72.66, 31.5) * mm, "end": v(72.66, 6.5) * mm});
            skPoint(sketch, "E52.0", {"position": v(90.66, 23) * mm});
            skCircle(sketch, "E53", {"center": v(90.66, 23) * mm, "radius": 1.5 * mm});
            skPoint(sketch, "E54.0", {"position": v(74.51, 24.9) * mm});
            skPoint(sketch, "E54.1", {"position": v(86.51, 22.15) * mm});
            skPoint(sketch, "E54.2", {"position": v(86.51, 14.15) * mm});
            skPoint(sketch, "E54.3", {"position": v(74.51, 11.4) * mm});
            skPoint(sketch, "E54.4", {"position": v(101.41, 22.15) * mm});
            skPoint(sketch, "E54.5", {"position": v(113.41, 26.65) * mm});
            skPoint(sketch, "E54.6", {"position": v(113.41, 14.15) * mm});
            skPoint(sketch, "E54.7", {"position": v(101.41, 9.65) * mm});
            skLineSegment(sketch, "E55.bottom", {"start": v(74.51, 24.9) * mm, "end": v(86.51, 24.9) * mm});
            skLineSegment(sketch, "E55.top", {"start": v(74.51, 22.15) * mm, "end": v(86.51, 22.15) * mm});
            skLineSegment(sketch, "E55.left", {"start": v(74.51, 24.9) * mm, "end": v(74.51, 22.15) * mm});
            skLineSegment(sketch, "E55.right", {"start": v(86.51, 24.9) * mm, "end": v(86.51, 22.15) * mm});
            skLineSegment(sketch, "E56.bottom", {"start": v(74.51, 11.4) * mm, "end": v(86.51, 11.4) * mm});
            skLineSegment(sketch, "E56.top", {"start": v(74.51, 14.15) * mm, "end": v(86.51, 14.15) * mm});
            skLineSegment(sketch, "E56.left", {"start": v(74.51, 11.4) * mm, "end": v(74.51, 14.15) * mm});
            skLineSegment(sketch, "E56.right", {"start": v(86.51, 11.4) * mm, "end": v(86.51, 14.15) * mm});
            skLineSegment(sketch, "E57.bottom", {"start": v(101.41, 22.15) * mm, "end": v(113.41, 22.15) * mm});
            skLineSegment(sketch, "E57.top", {"start": v(101.41, 26.65) * mm, "end": v(113.41, 26.65) * mm});
            skLineSegment(sketch, "E57.left", {"start": v(101.41, 22.15) * mm, "end": v(101.41, 26.65) * mm});
            skLineSegment(sketch, "E57.right", {"start": v(113.41, 22.15) * mm, "end": v(113.41, 26.65) * mm});
            skLineSegment(sketch, "E58.bottom", {"start": v(101.41, 9.65) * mm, "end": v(113.41, 9.65) * mm});
            skLineSegment(sketch, "E58.top", {"start": v(101.41, 14.15) * mm, "end": v(113.41, 14.15) * mm});
            skLineSegment(sketch, "E58.left", {"start": v(101.41, 9.65) * mm, "end": v(101.41, 14.15) * mm});
            skLineSegment(sketch, "E58.right", {"start": v(113.41, 9.65) * mm, "end": v(113.41, 14.15) * mm});
            skSolve(sketch);
        }
        {
            var Q0;
            Q0 = qSketchRegion(id + "F20", true);
            extrude(context, id + "F21", {"entities" : qUnion([Q0]), "operationType" : NewBodyOperationType.ADD, "depth" : 6.5 * mm});
        }
        {
            var Q0;
            Q0=makeQuery(id+"F2.opExtrude","CAP_FACE",FACE,{"disambiguationData":[OSD([sQuery(id+"F1.wireOp",EDGE,"E12.bottom"),sQuery(id+"F1.wireOp",EDGE,"E12.top"),sQuery(id+"F1.wireOp",EDGE,"E12.left"),sQuery(id+"F1.wireOp",EDGE,"E12.right"),sQuery(id+"F1.wireOp",EDGE,"E13.bottom"),sQuery(id+"F1.wireOp",EDGE,"E13.top"),sQuery(id+"F1.wireOp",EDGE,"E13.left"),sQuery(id+"F1.wireOp",EDGE,"E13.right"),sQuery(id+"F1.wireOp",EDGE,"E14"),sQuery(id+"F1.wireOp",EDGE,"E15"),sQuery(id+"F1.wireOp",EDGE,"E17.bottom"),sQuery(id+"F1.wireOp",EDGE,"E17.top"),sQuery(id+"F1.wireOp",EDGE,"E17.left"),sQuery(id+"F1.wireOp",EDGE,"E17.right"),sQuery(id+"F1.wireOp",EDGE,"E20"),sQuery(id+"F1.wireOp",EDGE,"E21.bottom"),sQuery(id+"F1.wireOp",EDGE,"E21.top"),sQuery(id+"F1.wireOp",EDGE,"E21.left"),sQuery(id+"F1.wireOp",EDGE,"E21.right"),sQuery(id+"F1.wireOp",EDGE,"E24.bottom"),sQuery(id+"F1.wireOp",EDGE,"E24.top"),sQuery(id+"F1.wireOp",EDGE,"E24.left"),sQuery(id+"F1.wireOp",EDGE,"E24.right"),sQuery(id+"F1.wireOp",EDGE,"E28.bottom"),sQuery(id+"F1.wireOp",EDGE,"E28.top"),sQuery(id+"F1.wireOp",EDGE,"E28.left"),sQuery(id+"F1.wireOp",EDGE,"E28.right"),sQuery(id+"F1.wireOp",EDGE,"E29.bottom"),sQuery(id+"F1.wireOp",EDGE,"E29.top"),sQuery(id+"F1.wireOp",EDGE,"E30.bottom"),sQuery(id+"F1.wireOp",EDGE,"E30.top"),sQuery(id+"F1.wireOp",EDGE,"E31.bottom"),sQuery(id+"F1.wireOp",EDGE,"E31.top")])],"isStart":false});
            var sketch = newSketch(context, id + "F22", { "sketchPlane" : qUnion([Q0])});
            skLineSegment(sketch, "E59.bottom", {"start": v(74.51, -11.4) * mm, "end": v(86.51, -11.4) * mm});
            skLineSegment(sketch, "E59.top", {"start": v(74.51, -24.9) * mm, "end": v(86.51, -24.9) * mm});
            skLineSegment(sketch, "E59.left", {"start": v(74.51, -11.4) * mm, "end": v(74.51, -24.9) * mm});
            skLineSegment(sketch, "E59.right", {"start": v(86.51, -11.4) * mm, "end": v(86.51, -24.9) * mm});
            skLineSegment(sketch, "E60.bottom", {"start": v(101.41, -9.65) * mm, "end": v(113.41, -9.65) * mm});
            skLineSegment(sketch, "E60.top", {"start": v(101.41, -26.65) * mm, "end": v(113.41, -26.65) * mm});
            skLineSegment(sketch, "E60.left", {"start": v(101.41, -9.65) * mm, "end": v(101.41, -26.65) * mm});
            skLineSegment(sketch, "E60.right", {"start": v(113.41, -9.65) * mm, "end": v(113.41, -26.65) * mm});
            skSolve(sketch);
        }
        {
            var Q0;
            Q0 = qSketchRegion(id + "F22", true);
            extrude(context, id + "F23", {"entities" : qUnion([Q0]), "operationType" : NewBodyOperationType.REMOVE, "oppositeDirection" : true, "depth" : 9 * mm});
        }
        {
            var Q0;
            Q0=makeQuery(id+"F9.imprint","IMPRINT",FACE,{"disambiguationData":[TD([[makeQuery(id+"F9.imprint","IMPRINT",EDGE,{"derivedFrom":sQuery(id+"F9.wireOp",EDGE,"E36.top")}),1.0]])]});
            var sketch = newSketch(context, id + "F26", { "sketchPlane" : qUnion([Q0])});
            skPoint(sketch, "E61.0", {"position": v(20.5, 8.5) * mm});
            skCircle(sketch, "E62", {"center": v(20.5, 8.5) * mm, "radius": 3.75 * mm});
            skSolve(sketch);
        }
        {
            var Q0;
            Q0 = qSketchRegion(id + "F26", true);
            extrude(context, id + "F27", {"entities" : qUnion([Q0]), "operationType" : NewBodyOperationType.REMOVE, "oppositeDirection" : true, "depth" : 1 * mm});
        }
    });
